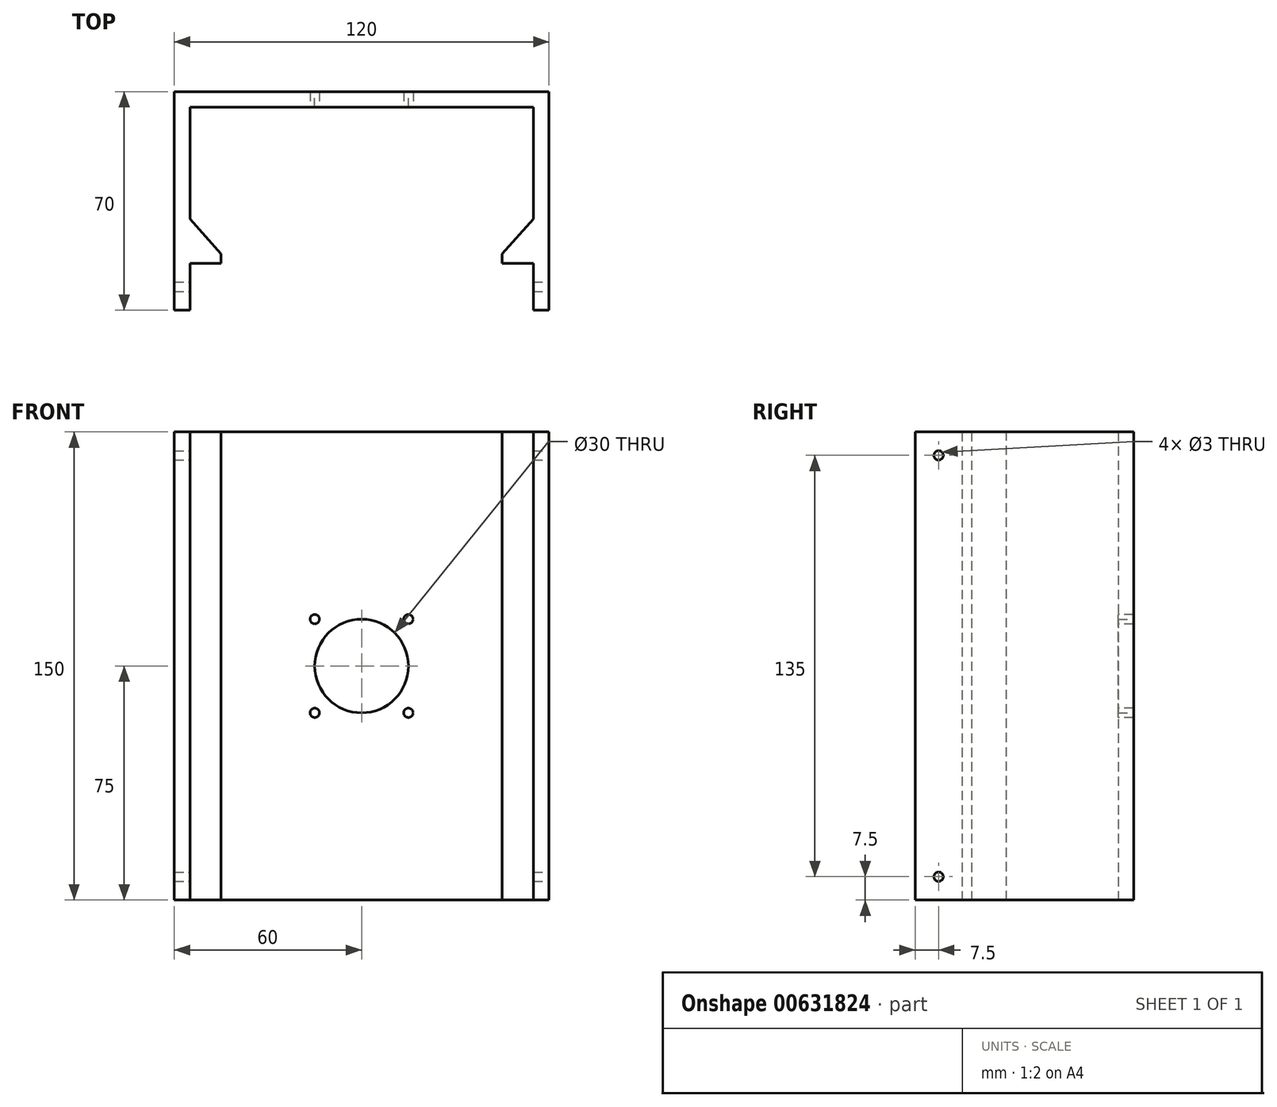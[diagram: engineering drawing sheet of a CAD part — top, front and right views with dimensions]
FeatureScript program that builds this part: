
annotation { "Feature Type Name" : "Feature", "Feature Type Description" : "" }
export const myFeature = defineFeature(function(context is Context, id is Id, definition is map)
    precondition{}
    {
        {
            var Q0;
            Q0=qCreatedBy(makeId("Front.planeOp"),FACE);
            var sketch = newSketch(context, id + "F0", { "sketchPlane" : qUnion([Q0])});
            skLineSegment(sketch, "E0.bottom", {"start": v(-60, -75) * mm, "end": v(60, -75) * mm});
            skLineSegment(sketch, "E0.top", {"start": v(-60, 75) * mm, "end": v(60, 75) * mm});
            skLineSegment(sketch, "E0.left", {"start": v(-60, -75) * mm, "end": v(-60, 75) * mm});
            skLineSegment(sketch, "E0.right", {"start": v(60, -75) * mm, "end": v(60, 75) * mm});
            skPoint(sketch, "E0.middle", {"position": v(0, 0) * mm});
            skSolve(sketch);
        }
        {
            var Q0;
            Q0 = qSketchRegion(id + "F0", true);
            extrude(context, id + "F1", {"entities" : qUnion([Q0]), "depth" : 5 * mm, "offsetDistance" : 25 * mm});
        }
        {
            var Q0;
            Q0=makeQuery(id+"F1.opExtrude","CAP_FACE",FACE,{"disambiguationData":[OSD([sQuery(id+"F0.wireOp",EDGE,"E0.bottom"),sQuery(id+"F0.wireOp",EDGE,"E0.top"),sQuery(id+"F0.wireOp",EDGE,"E0.left"),sQuery(id+"F0.wireOp",EDGE,"E0.right")])],"isStart":false});
            var sketch = newSketch(context, id + "F2", { "sketchPlane" : qUnion([Q0])});
            skLineSegment(sketch, "E1.bottom", {"start": v(-60, 75) * mm, "end": v(-55, 75) * mm});
            skLineSegment(sketch, "E1.top", {"start": v(-60, -75) * mm, "end": v(-55, -75) * mm});
            skLineSegment(sketch, "E1.left", {"start": v(-60, 75) * mm, "end": v(-60, -75) * mm});
            skLineSegment(sketch, "E1.right", {"start": v(-55, 75) * mm, "end": v(-55, -75) * mm});
            skLineSegment(sketch, "E2.bottom", {"start": v(60, 75) * mm, "end": v(55, 75) * mm});
            skLineSegment(sketch, "E2.top", {"start": v(60, -75) * mm, "end": v(55, -75) * mm});
            skLineSegment(sketch, "E2.left", {"start": v(60, 75) * mm, "end": v(60, -75) * mm});
            skLineSegment(sketch, "E2.right", {"start": v(55, 75) * mm, "end": v(55, -75) * mm});
            skSolve(sketch);
        }
        {
            var Q0;
            Q0 = qSketchRegion(id + "F2", true);
            extrude(context, id + "F3", {"entities" : qUnion([Q0]), "operationType" : NewBodyOperationType.ADD, "depth" : 65 * mm, "offsetDistance" : 25 * mm});
        }
        {
            var Q0;
            Q0=makeQuery(id+"F3.opExtrude","SWEPT_FACE",FACE,{"disambiguationData":[OSD([sQuery(id+"F2.wireOp",EDGE,"E2.right")])]});
            var sketch = newSketch(context, id + "F4", { "sketchPlane" : qUnion([Q0])});
            skLineSegment(sketch, "E3", {"start": v(70, 75) * mm, "end": v(55, 75) * mm, "construction": true});
            skLineSegment(sketch, "E4.bottom", {"start": v(55, 75) * mm, "end": v(52, 75) * mm});
            skLineSegment(sketch, "E4.top", {"start": v(55, -75) * mm, "end": v(52, -75) * mm});
            skLineSegment(sketch, "E4.left", {"start": v(55, 75) * mm, "end": v(55, -75) * mm});
            skLineSegment(sketch, "E4.right", {"start": v(52, 75) * mm, "end": v(52, -75) * mm});
            skSolve(sketch);
        }
        {
            var Q0;
            Q0 = qSketchRegion(id + "F4", true);
            extrude(context, id + "F5", {"entities" : qUnion([Q0]), "operationType" : NewBodyOperationType.ADD, "depth" : 10 * mm, "offsetDistance" : 25 * mm});
        }
        {
            var Q0;
            Q0=makeQuery(id+"F3.opExtrude","SWEPT_FACE",FACE,{"disambiguationData":[OSD([sQuery(id+"F2.wireOp",EDGE,"E1.right")])]});
            var sketch = newSketch(context, id + "F6", { "sketchPlane" : qUnion([Q0])});
            skLineSegment(sketch, "E5", {"start": v(-70, 75) * mm, "end": v(-55, 75) * mm, "construction": true});
            skLineSegment(sketch, "E6.bottom", {"start": v(-55, 75) * mm, "end": v(-52, 75) * mm});
            skLineSegment(sketch, "E6.top", {"start": v(-55, -75) * mm, "end": v(-52, -75) * mm});
            skLineSegment(sketch, "E6.left", {"start": v(-55, 75) * mm, "end": v(-55, -75) * mm});
            skLineSegment(sketch, "E6.right", {"start": v(-52, 75) * mm, "end": v(-52, -75) * mm});
            skSolve(sketch);
        }
        {
            var Q0;
            Q0 = qSketchRegion(id + "F6", true);
            extrude(context, id + "F7", {"entities" : qUnion([Q0]), "operationType" : NewBodyOperationType.ADD, "depth" : 10 * mm, "offsetDistance" : 25 * mm});
        }
        {
            var Q0;
            Q0=makeQuery(id+"F7.boolean.opBoolean","MERGE",FACE,{"derivedFrom":[makeQuery(id+"F5.boolean.opBoolean","MERGE",FACE,{"derivedFrom":[makeQuery(id+"F3.boolean.opBoolean","MERGE",FACE,{"derivedFrom":[makeQuery(id+"F1.opExtrude","SWEPT_FACE",FACE,{"disambiguationData":[OSD([sQuery(id+"F0.wireOp",EDGE,"E0.top")])]}),makeQuery(id+"F3.opExtrude","SWEPT_FACE",FACE,{"disambiguationData":[OSD([sQuery(id+"F2.wireOp",EDGE,"E1.bottom")])]}),makeQuery(id+"F3.opExtrude","SWEPT_FACE",FACE,{"disambiguationData":[OSD([sQuery(id+"F2.wireOp",EDGE,"E2.bottom")])]})]}),makeQuery(id+"F5.opExtrude","SWEPT_FACE",FACE,{"disambiguationData":[OSD([sQuery(id+"F4.wireOp",EDGE,"E4.bottom")])]})]}),makeQuery(id+"F7.opExtrude","SWEPT_FACE",FACE,{"disambiguationData":[OSD([sQuery(id+"F6.wireOp",EDGE,"E6.bottom")])]})]});
            var sketch = newSketch(context, id + "F8", { "sketchPlane" : qUnion([Q0])});
            skLineSegment(sketch, "E7", {"start": v(45, -52) * mm, "end": v(55, -40.82) * mm});
            skLineSegment(sketch, "E8", {"start": v(55, -40.82) * mm, "end": v(55, -52) * mm});
            skLineSegment(sketch, "E9", {"start": v(55, -52) * mm, "end": v(45, -52) * mm});
            skLineSegment(sketch, "E10", {"start": v(-45, -52) * mm, "end": v(-55, -40.82) * mm});
            skLineSegment(sketch, "E11", {"start": v(-55, -40.82) * mm, "end": v(-55, -52) * mm});
            skLineSegment(sketch, "E12", {"start": v(-55, -52) * mm, "end": v(-45, -52) * mm});
            skSolve(sketch);
        }
        {
            var Q0;
            Q0=makeQuery(id+"F8.imprint","IMPRINT",FACE,{"disambiguationData":[TD([[makeQuery(id+"F8.imprint","IMPRINT",EDGE,{"derivedFrom":sQuery(id+"F8.wireOp",EDGE,"E7")}),-1.0]])]});
            extrude(context, id + "F9", {"entities" : qUnion([Q0]), "operationType" : NewBodyOperationType.ADD, "oppositeDirection" : true, "depth" : 150 * mm, "offsetDistance" : 25 * mm});
        }
        {
            var Q0;
            Q0 = qSketchRegion(id + "F8", true);
            extrude(context, id + "F10", {"entities" : qUnion([Q0]), "operationType" : NewBodyOperationType.ADD, "oppositeDirection" : true, "depth" : 150 * mm, "offsetDistance" : 25 * mm});
        }
        {
            var Q0;
            {var subQ0=sQuery(id+"F2.wireOp",EDGE,"E1.right");Q0=makeQuery(id+"F2.imprint","IMPRINT",FACE,{"disambiguationData":[TD([[makeQuery(id+"F2.imprint","IMPRINT",EDGE,{"derivedFrom":subQ0}),1.0]])]});}
            var sketch = newSketch(context, id + "F11", { "sketchPlane" : qUnion([Q0])});
            skCircle(sketch, "E13", {"center": v(0, 0) * mm, "radius": 15 * mm});
            skLineSegment(sketch, "E14.bottom", {"start": v(15, -15) * mm, "end": v(-15, -15) * mm});
            skLineSegment(sketch, "E14.top", {"start": v(15, 15) * mm, "end": v(-15, 15) * mm});
            skLineSegment(sketch, "E14.left", {"start": v(15, -15) * mm, "end": v(15, 15) * mm});
            skLineSegment(sketch, "E14.right", {"start": v(-15, -15) * mm, "end": v(-15, 15) * mm});
            skCircle(sketch, "E15", {"center": v(-15, -15) * mm, "radius": 1.5 * mm});
            skCircle(sketch, "E16", {"center": v(15, -15) * mm, "radius": 1.5 * mm});
            skCircle(sketch, "E17", {"center": v(15, 15) * mm, "radius": 1.5 * mm});
            skCircle(sketch, "E18", {"center": v(-15, 15) * mm, "radius": 1.5 * mm});
            skSolve(sketch);
        }
        {
            var Q0;
            Q0=sQuery(id+"F11.wireOp",VERTEX,"E14.right.end");
            var Q1;
            Q1=sQuery(id+"F0.wireOp",VERTEX,"E0.middle");
            var Q2;
            Q2=sQuery(id+"F11.wireOp",VERTEX,"E15.center");
            var Q3;
            Q3=sQuery(id+"F11.wireOp",VERTEX,"E16.center");
            var Q4;
            Q4=sQuery(id+"F11.wireOp",VERTEX,"E14.left.end");
            var Q5;
            Q5=makeQuery(id+"F1.opExtrude","SWEPT_BODY",BODY,{"disambiguationData":[OSD([sQuery(id+"F0.wireOp",EDGE,"E0.bottom"),sQuery(id+"F0.wireOp",EDGE,"E0.top"),sQuery(id+"F0.wireOp",EDGE,"E0.left"),sQuery(id+"F0.wireOp",EDGE,"E0.right")])]});
            hole(context, id + "F12", {"style" : HoleStyle.SIMPLE, "endStyle" : HoleEndStyle.THROUGH, "holeDiameter" : 3 * mm, "majorDiameter" : 5 * mm, "isTappedThrough" : true, "tappedDepth" : 12 * mm, "tapClearance" : 3, "locations" : qUnion([Q0, Q1, Q2, Q3, Q4]), "scope" : qUnion([Q5])});
        }
        {
            var Q0;
            Q0=sQuery(id+"F0.wireOp",VERTEX,"E0.middle");
            var Q1;
            Q1=makeQuery(id+"F1.opExtrude","SWEPT_BODY",BODY,{"disambiguationData":[OSD([sQuery(id+"F0.wireOp",EDGE,"E0.bottom"),sQuery(id+"F0.wireOp",EDGE,"E0.top"),sQuery(id+"F0.wireOp",EDGE,"E0.left"),sQuery(id+"F0.wireOp",EDGE,"E0.right")])]});
            hole(context, id + "F13", {"style" : HoleStyle.SIMPLE, "endStyle" : HoleEndStyle.THROUGH, "oppositeDirection" : true, "holeDiameter" : 30 * mm, "majorDiameter" : 5 * mm, "isTappedThrough" : true, "tappedDepth" : 12 * mm, "tapClearance" : 3, "locations" : qUnion([Q0]), "scope" : qUnion([Q1])});
        }
        {
            var Q0;
            Q0=makeQuery(id+"F3.boolean.opBoolean","MERGE",FACE,{"derivedFrom":[makeQuery(id+"F1.opExtrude","SWEPT_FACE",FACE,{"disambiguationData":[OSD([sQuery(id+"F0.wireOp",EDGE,"E0.right")])]}),makeQuery(id+"F3.opExtrude","SWEPT_FACE",FACE,{"disambiguationData":[OSD([sQuery(id+"F2.wireOp",EDGE,"E2.left")])]})]});
            var sketch = newSketch(context, id + "F14", { "sketchPlane" : qUnion([Q0])});
            skLineSegment(sketch, "E19.bottom", {"start": v(-70, -75) * mm, "end": v(-55, -75) * mm});
            skLineSegment(sketch, "E19.top", {"start": v(-70, -60) * mm, "end": v(-55, -60) * mm});
            skLineSegment(sketch, "E19.left", {"start": v(-70, -75) * mm, "end": v(-70, -60) * mm});
            skLineSegment(sketch, "E19.right", {"start": v(-55, -75) * mm, "end": v(-55, -60) * mm});
            skLineSegment(sketch, "E20.bottom", {"start": v(-70, 75) * mm, "end": v(-55, 75) * mm});
            skLineSegment(sketch, "E20.top", {"start": v(-70, 60) * mm, "end": v(-55, 60) * mm});
            skLineSegment(sketch, "E20.left", {"start": v(-70, 75) * mm, "end": v(-70, 60) * mm});
            skLineSegment(sketch, "E20.right", {"start": v(-55, 75) * mm, "end": v(-55, 60) * mm});
            skLineSegment(sketch, "E21", {"start": v(-70, -75) * mm, "end": v(-55, -60) * mm});
            skLineSegment(sketch, "E22", {"start": v(-70, -60) * mm, "end": v(-55, -75) * mm});
            skLineSegment(sketch, "E23", {"start": v(-55, 60) * mm, "end": v(-70, 75) * mm});
            skLineSegment(sketch, "E24", {"start": v(-70, 60) * mm, "end": v(-55, 75) * mm});
            skPoint(sketch, "E25", {"position": v(-62.5, 67.5) * mm});
            skPoint(sketch, "E26", {"position": v(-62.5, -67.5) * mm});
            skSolve(sketch);
        }
        {
            var Q0;
            Q0=sQuery(id+"F14.wireOp",VERTEX,"E26");
            var Q1;
            Q1=sQuery(id+"F14.wireOp",VERTEX,"E25");
            var Q2;
            Q2=makeQuery(id+"F1.opExtrude","SWEPT_BODY",BODY,{"disambiguationData":[OSD([sQuery(id+"F0.wireOp",EDGE,"E0.bottom"),sQuery(id+"F0.wireOp",EDGE,"E0.top"),sQuery(id+"F0.wireOp",EDGE,"E0.left"),sQuery(id+"F0.wireOp",EDGE,"E0.right")])]});
            hole(context, id + "F15", {"style" : HoleStyle.SIMPLE, "endStyle" : HoleEndStyle.THROUGH, "holeDiameter" : 3 * mm, "majorDiameter" : 5 * mm, "isTappedThrough" : true, "tappedDepth" : 12 * mm, "tapClearance" : 3, "locations" : qUnion([Q0, Q1]), "scope" : qUnion([Q2])});
        }
    });
